# Revit family: Geräteeinsätze GES_Geräteeinsatz_Revisionsabdeckung ZESR7
name_source: partatom
category: Generic Models
revit_build: Autodesk Revit 2015 (Build: 20140606_1530(x64)
units: mm (PartAtom-declared; Revit-internal decimal feet)

## types (3) — shared parameters
Bodenbelagdicke = 10 mm  [stored 0.0328084 ft]
Diameter dimesion = 274 mm  [stored 0.89895 ft]
Height = 35 mm  [stored 0.114829 ft]
Inner cut = 266 mm  [stored 0.872703 ft]
Inner cut 3 = 165 mm
Inner cut2 = 230 mm  [stored 0.754593 ft]
Manufacturer = OBO Bettermann
Outer Diameter Dimension = 294 mm  [stored 0.964567 ft]
URL = http://www.obo-bettermann.com

## per-type parameters (varying)
| type | GTIN | Manufacturer Art. No. | Material |
| ZESR7 10U 7011 | 4012195109600 | 7406788 | Plastic RAL 7011 |
| ZESR7 10U 9011 | 4012195109617 | 7406792 | Plastic RAL 9011 |
| ZESR7 10U 1019 | 4012195109624 | 7406796 | Plastic RAL 1019 |

note: column(s) folded — value = type name in every type: Article Type

note: [stored X ft] marks values corroborated as IEEE doubles in the binary element streams (Revit-internal decimal feet)

## geometry (parser evidence)
native form markers: Sweep x2
no freeform markers — native parametric forms only
